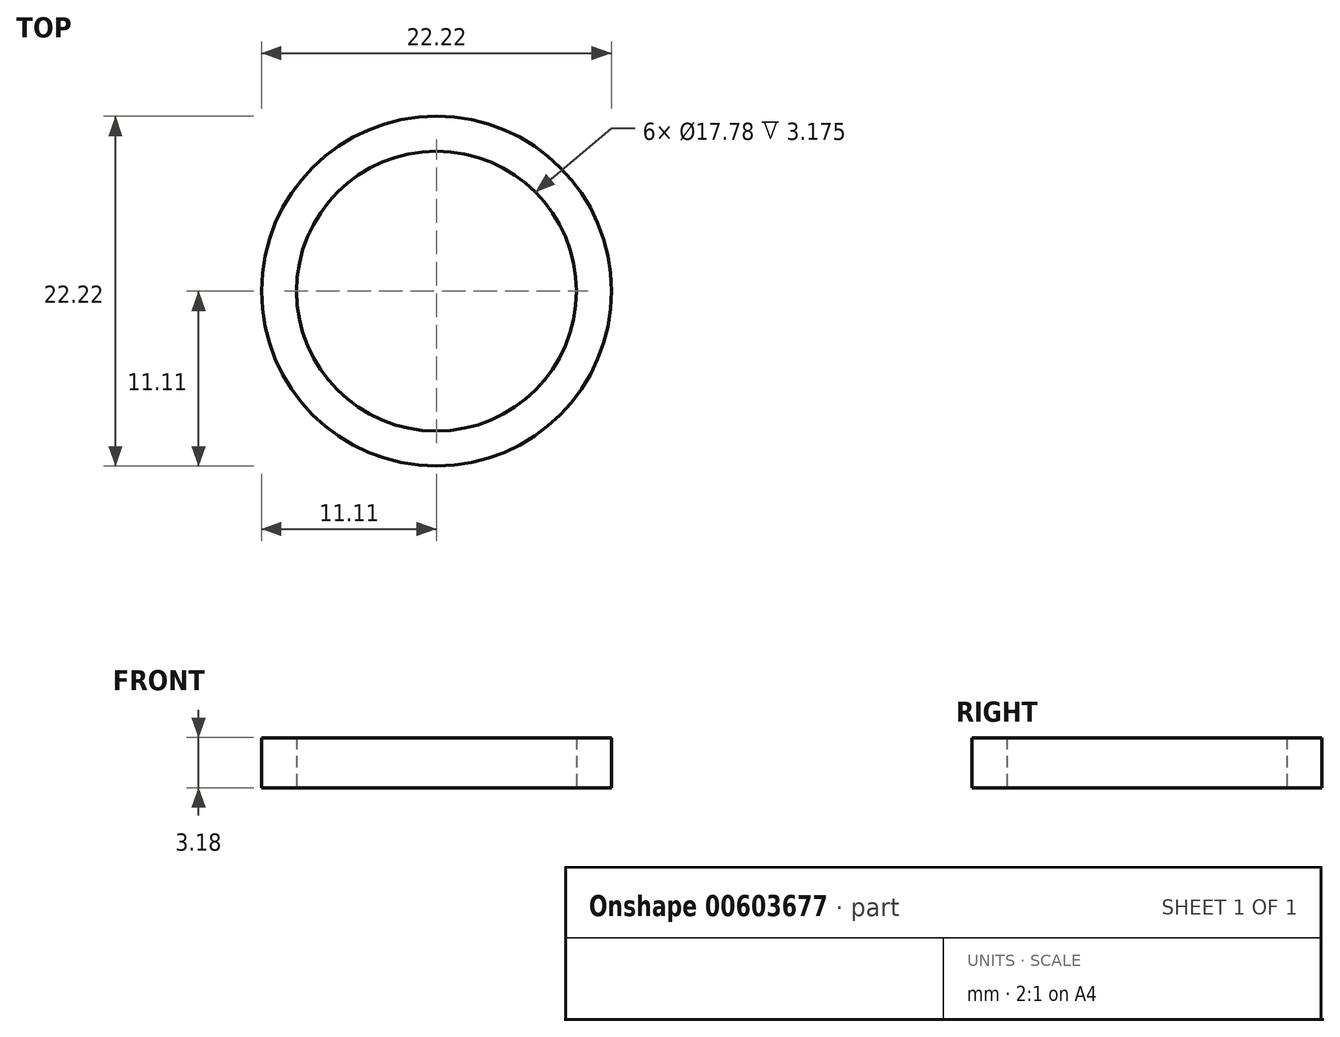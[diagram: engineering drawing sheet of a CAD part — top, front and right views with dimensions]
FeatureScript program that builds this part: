
annotation { "Feature Type Name" : "Feature", "Feature Type Description" : "" }
export const myFeature = defineFeature(function(context is Context, id is Id, definition is map)
    precondition{}
    {
        {
            var Q0;
            Q0=qCreatedBy(makeId("Top.planeOp"),FACE);
            var sketch = newSketch(context, id + "F0", { "sketchPlane" : qUnion([Q0])});
            skCircle(sketch, "E0", {"center": v(0, 0) * mm, "radius": 8.9 * mm});
            skCircle(sketch, "E1", {"center": v(0, 0) * mm, "radius": 11.11 * mm});
            skSolve(sketch);
        }
        {
            var Q0;
            Q0 = qSketchRegion(id + "F0", true);
            extrude(context, id + "F1", {"entities" : qUnion([Q0]), "depth" : 3.17 * mm, "offsetDistance" : 25.4 * mm});
        }
    });
